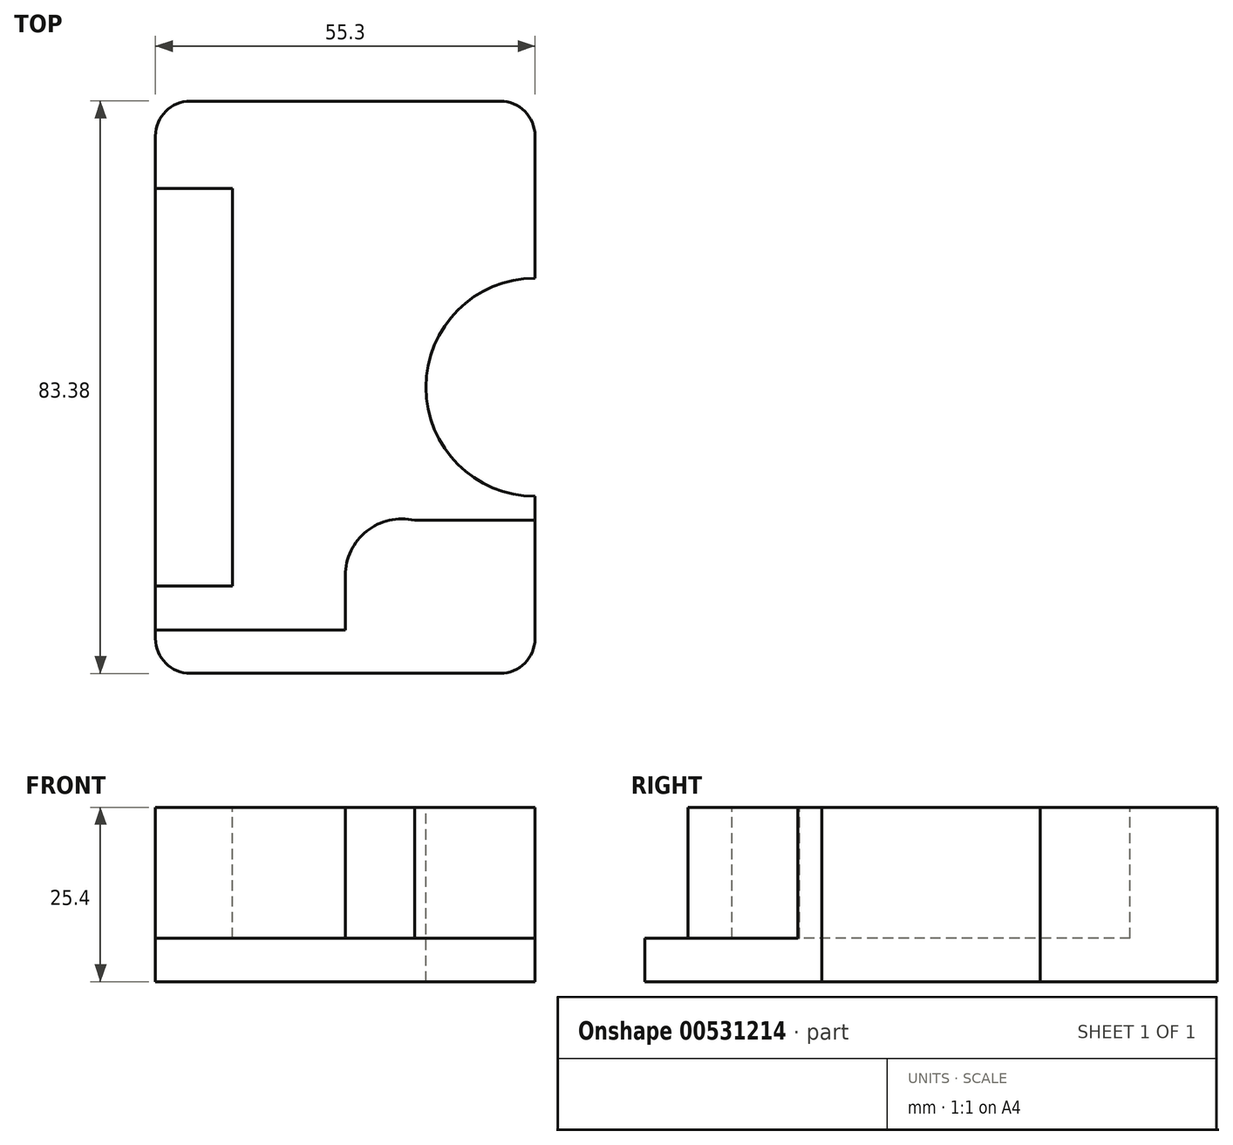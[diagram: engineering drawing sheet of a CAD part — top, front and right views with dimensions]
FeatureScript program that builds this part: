
annotation { "Feature Type Name" : "Feature", "Feature Type Description" : "" }
export const myFeature = defineFeature(function(context is Context, id is Id, definition is map)
    precondition{}
    {
        {
            var Q0;
            Q0=qCreatedBy(makeId("Top.planeOp"),FACE);
            var sketch = newSketch(context, id + "F0", { "sketchPlane" : qUnion([Q0])});
            skLineSegment(sketch, "E0.bottom", {"start": v(-27.65, 41.69) * mm, "end": v(27.65, 41.69) * mm});
            skLineSegment(sketch, "E0.top", {"start": v(-27.65, -41.69) * mm, "end": v(27.65, -41.69) * mm});
            skLineSegment(sketch, "E0.left", {"start": v(-27.65, 41.69) * mm, "end": v(-27.65, -41.69) * mm});
            skLineSegment(sketch, "E0.right", {"start": v(27.65, 41.69) * mm, "end": v(27.65, -41.69) * mm});
            skPoint(sketch, "E0.middle", {"position": v(0, 0) * mm});
            skSolve(sketch);
        }
        {
            var Q0;
            Q0 = qSketchRegion(id + "F0", true);
            extrude(context, id + "F1", {"entities" : qUnion([Q0]), "depth" : 25.4 * mm, "offsetDistance" : 25.4 * mm});
        }
        {
            var Q0;
            Q0=makeQuery(id+"F1.opExtrude","CAP_FACE",FACE,{"disambiguationData":[OSD([sQuery(id+"F0.wireOp",EDGE,"E0.bottom"),sQuery(id+"F0.wireOp",EDGE,"E0.top"),sQuery(id+"F0.wireOp",EDGE,"E0.left"),sQuery(id+"F0.wireOp",EDGE,"E0.right")])],"isStart":false});
            var sketch = newSketch(context, id + "F2", { "sketchPlane" : qUnion([Q0])});
            skCircle(sketch, "E1", {"center": v(27.65, 0) * mm, "radius": 15.9 * mm});
            skSolve(sketch);
        }
        {
            var Q0;
            Q0 = qSketchRegion(id + "F2", true);
            extrude(context, id + "F3", {"entities" : qUnion([Q0]), "operationType" : NewBodyOperationType.REMOVE, "endBound" : BoundingType.THROUGH_ALL, "oppositeDirection" : true, "depth" : 25.4 * mm, "offsetDistance" : 25.4 * mm});
        }
        {
            var Q0;
            Q0=makeQuery(id+"F1.opExtrude","CAP_FACE",FACE,{"disambiguationData":[OSD([sQuery(id+"F0.wireOp",EDGE,"E0.bottom"),sQuery(id+"F0.wireOp",EDGE,"E0.top"),sQuery(id+"F0.wireOp",EDGE,"E0.left"),sQuery(id+"F0.wireOp",EDGE,"E0.right")])],"isStart":false});
            var sketch = newSketch(context, id + "F4", { "sketchPlane" : qUnion([Q0])});
            skLineSegment(sketch, "E2.bottom", {"start": v(-27.65, 28.99) * mm, "end": v(-16.43, 28.99) * mm});
            skLineSegment(sketch, "E2.top", {"start": v(-27.65, -28.99) * mm, "end": v(-16.43, -28.99) * mm});
            skLineSegment(sketch, "E2.left", {"start": v(-27.65, 28.99) * mm, "end": v(-27.65, -28.99) * mm});
            skLineSegment(sketch, "E2.right", {"start": v(-16.43, 28.99) * mm, "end": v(-16.43, -28.99) * mm});
            skSolve(sketch);
        }
        {
            var Q0;
            Q0 = qSketchRegion(id + "F4", true);
            extrude(context, id + "F5", {"entities" : qUnion([Q0]), "operationType" : NewBodyOperationType.REMOVE, "oppositeDirection" : true, "depth" : 19.05 * mm, "offsetDistance" : 25.4 * mm});
        }
        {
            var Q0;
            Q0=makeQuery(id+"F1.opExtrude","CAP_FACE",FACE,{"disambiguationData":[OSD([sQuery(id+"F0.wireOp",EDGE,"E0.bottom"),sQuery(id+"F0.wireOp",EDGE,"E0.top"),sQuery(id+"F0.wireOp",EDGE,"E0.left"),sQuery(id+"F0.wireOp",EDGE,"E0.right")])],"isStart":false});
            var sketch = newSketch(context, id + "F6", { "sketchPlane" : qUnion([Q0])});
            skLineSegment(sketch, "E3", {"start": v(27.65, -19.38) * mm, "end": v(10.1, -19.38) * mm});
            skPoint(sketch, "E4.endSnap0", {"position": v(0, -41.69) * mm});
            skArc(sketch, "E5", {"start": v(0, -27.4) * mm, "mid": v(3.11, -20.96) * mm, "end": v(10.1, -19.38) * mm});
            skLineSegment(sketch, "E6", {"start": v(0, -27.4) * mm, "end": v(0, -35.38) * mm});
            skLineSegment(sketch, "E7", {"start": v(0, -35.38) * mm, "end": v(-27.65, -35.38) * mm});
            skLineSegment(sketch, "E8", {"start": v(-27.65, -35.38) * mm, "end": v(-27.65, -41.69) * mm});
            skLineSegment(sketch, "E9", {"start": v(-27.65, -41.69) * mm, "end": v(27.65, -41.69) * mm});
            skLineSegment(sketch, "E10", {"start": v(27.65, -41.69) * mm, "end": v(27.65, -19.38) * mm});
            skSolve(sketch);
        }
        {
            var Q0;
            Q0 = qSketchRegion(id + "F6", true);
            extrude(context, id + "F7", {"entities" : qUnion([Q0]), "operationType" : NewBodyOperationType.REMOVE, "oppositeDirection" : true, "depth" : 19.05 * mm, "offsetDistance" : 25.4 * mm});
        }
        {
            var Q0;
            Q0=makeQuery(id+"F1.opExtrude","SWEPT_EDGE",EDGE,{"disambiguationData":[OSD([sQuery(id+"F0.wireOp",EDGE,"E0.top"),sQuery(id+"F0.wireOp",EDGE,"E0.right")])]});
            var Q1;
            Q1=makeQuery(id+"F1.opExtrude","SWEPT_EDGE",EDGE,{"disambiguationData":[OSD([sQuery(id+"F0.wireOp",EDGE,"E0.bottom"),sQuery(id+"F0.wireOp",EDGE,"E0.right")])]});
            var Q2;
            Q2=makeQuery(id+"F1.opExtrude","SWEPT_EDGE",EDGE,{"disambiguationData":[OSD([sQuery(id+"F0.wireOp",EDGE,"E0.bottom"),sQuery(id+"F0.wireOp",EDGE,"E0.left")])]});
            var Q3;
            Q3=makeQuery(id+"F1.opExtrude","SWEPT_EDGE",EDGE,{"disambiguationData":[OSD([sQuery(id+"F0.wireOp",EDGE,"E0.top"),sQuery(id+"F0.wireOp",EDGE,"E0.left")])]});
            fillet(context, id + "F8", {"entities" : qUnion([Q0, Q1, Q2, Q3]), "radius" : 5.08 * mm, "tangentPropagation" : true, "allowEdgeOverflow" : false});
        }
    });
